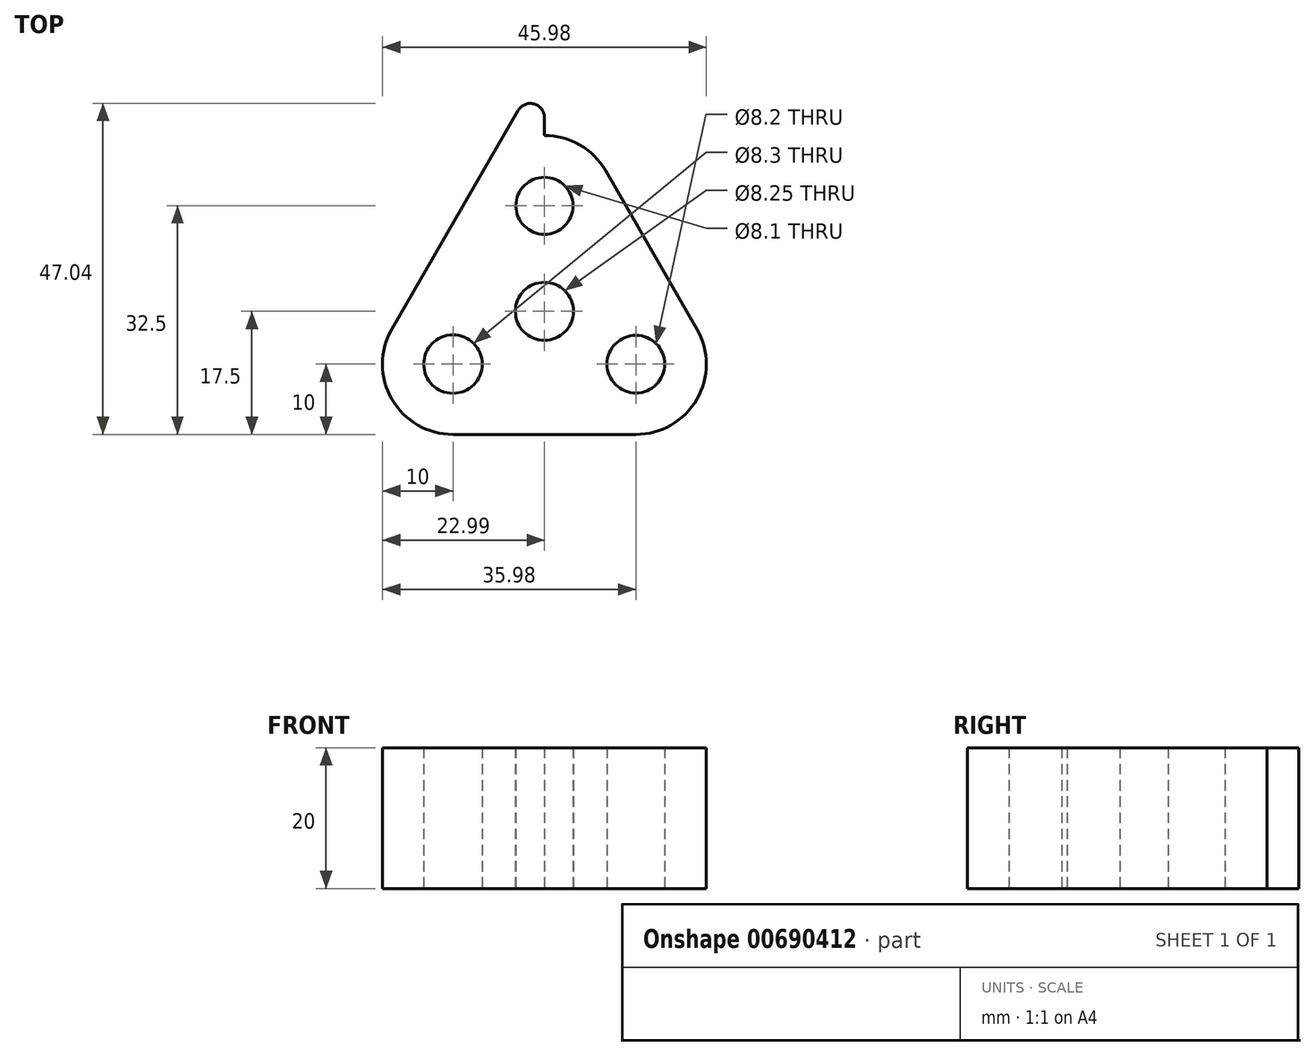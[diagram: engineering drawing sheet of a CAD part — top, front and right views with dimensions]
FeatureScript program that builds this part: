
annotation { "Feature Type Name" : "Feature", "Feature Type Description" : "" }
export const myFeature = defineFeature(function(context is Context, id is Id, definition is map)
    precondition{}
    {
        {
            var Q0;
            Q0=qCreatedBy(makeId("Top.planeOp"),FACE);
            var sketch = newSketch(context, id + "F0", { "sketchPlane" : qUnion([Q0])});
            skCircle(sketch, "E0", {"center": v(0, 15) * mm, "radius": 4.05 * mm});
            skLineSegment(sketch, "E1", {"start": v(-8.66, 20) * mm, "end": v(-21.65, -2.5) * mm});
            skLineSegment(sketch, "E2", {"start": v(-13, -17.5) * mm, "end": v(13, -17.5) * mm});
            skLineSegment(sketch, "E3", {"start": v(21.65, -2.5) * mm, "end": v(8.66, 20) * mm});
            skPoint(sketch, "E4", {"position": v(0, -17.5) * mm});
            skLineSegment(sketch, "E5", {"start": v(15.16, 8.75) * mm, "end": v(-30.31, -17.5) * mm, "construction": true});
            skLineSegment(sketch, "E6", {"start": v(30.31, -17.5) * mm, "end": v(-15.16, 8.75) * mm, "construction": true});
            skPoint(sketch, "E7.visualSharp", {"position": v(0, 35) * mm});
            skArc(sketch, "E7.filletArc", {"start": v(8.66, 20) * mm, "mid": v(0, 25) * mm, "end": v(-8.66, 20) * mm});
            skPoint(sketch, "E8.visualSharp", {"position": v(30.31, -17.5) * mm});
            skArc(sketch, "E8.filletArc", {"start": v(13, -17.5) * mm, "mid": v(21.65, -12.5) * mm, "end": v(21.65, -2.5) * mm});
            skPoint(sketch, "E9.visualSharp", {"position": v(-30.31, -17.5) * mm});
            skArc(sketch, "E9.filletArc", {"start": v(-21.65, -2.5) * mm, "mid": v(-21.65, -12.5) * mm, "end": v(-13, -17.5) * mm});
            skCircle(sketch, "E10", {"center": v(13, -7.5) * mm, "radius": 4.1 * mm});
            skCircle(sketch, "E11", {"center": v(-13, -7.5) * mm, "radius": 4.15 * mm});
            skCircle(sketch, "E12", {"center": v(0, 0) * mm, "radius": 4.12 * mm});
            skLineSegment(sketch, "E13", {"start": v(0, 15) * mm, "end": v(-13, -7.5) * mm, "construction": true});
            skLineSegment(sketch, "E14", {"start": v(13, -7.5) * mm, "end": v(0, 15) * mm, "construction": true});
            skLineSegment(sketch, "E15", {"start": v(13, -7.5) * mm, "end": v(-13, -7.5) * mm, "construction": true});
            skLineSegment(sketch, "E16", {"start": v(-8.66, 20) * mm, "end": v(0, 35) * mm});
            skLineSegment(sketch, "E17", {"start": v(0, 25) * mm, "end": v(0, 35) * mm});
            skSolve(sketch);
        }
        {
            var Q0;
            Q0 = qSketchRegion(id + "F0", true);
            extrude(context, id + "F1", {"entities" : qUnion([Q0]), "depth" : 20 * mm, "offsetDistance" : 25 * mm});
        }
        {
            var Q0;
            Q0=makeQuery(id+"F1.opExtrude","SWEPT_EDGE",EDGE,{"disambiguationData":[OSD([sQuery(id+"F0.wireOp",EDGE,"E16"),sQuery(id+"F0.wireOp",EDGE,"E17")])]});
            fillet(context, id + "F2", {"entities" : qUnion([Q0]), "radius" : 2 * mm, "tangentPropagation" : true, "allowEdgeOverflow" : false});
        }
    });
